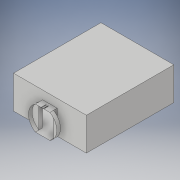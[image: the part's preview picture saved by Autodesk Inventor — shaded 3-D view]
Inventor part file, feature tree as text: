
AUTODESK INVENTOR PART (.ipt)
format: ipt  version: 2017 (Build 210142000, 142)  size: 224,256 bytes
history: native  units: in
note: dims shown in document units (in); Inventor stores cm internally (conversion verified against a paired STEP export)
features: extrude x6, sketch x5, delete_face x1
ambient origin geometry x8: Origin, YZ Plane, XZ Plane, XY Plane, X Axis, Y Axis, Z Axis, Center Point
bodies: Solid1 (feature_tree)
feature tree (12):
  extrude  "floor"  Depth=22.0in
  extrude  "walls"  Depth=1.0in
  extrude  "doorframe"  Depth=1.0in
  extrude  "ceiling"  Depth=1.0in TaperAngle=0.0deg
  sketch  "Sketch10"  dims[d17=2.0in d18=6.6667in d20=8.6667in d21=0.0in d22=1.0in d23=0.0in d37=6.6667in d40=1.0in d41=0.0in d46=0.25in d47=0.125in d48=45.0deg d49=0.0892in d50=0.0884in d53=0.25in d54=0.0in d63=4.0in d64=0.5833in d65=3.8873in d66=3.8873in d67=1.7083in d68=0.0625in d69=0.0625in d70=1.6458in d71=0.25in d72=0.125in d73=0.0884in d74=45.0deg d75=3.3333in d76=1.0in d77=1.0in d78=0.125in]
  extrude  "corridor connect"  Depth=6.6667in
  extrude  "reveil rest of light"  Depth=1.0in TaperAngle=0.0deg
  delete_face  "Delete Face1"
  sketch  "Sketch1"  dims[d0=22.0in d1=26.0in]
  sketch  "Sketch4"  dims[d2=1.0in d3=0.0in d11=1.0in]
  sketch  "Sketch5"  dims[d12=1.0in d13=1.0in]
  sketch  "Sketch7"  dims[d14=1.0in d15=10.0in d16=0.0in]
